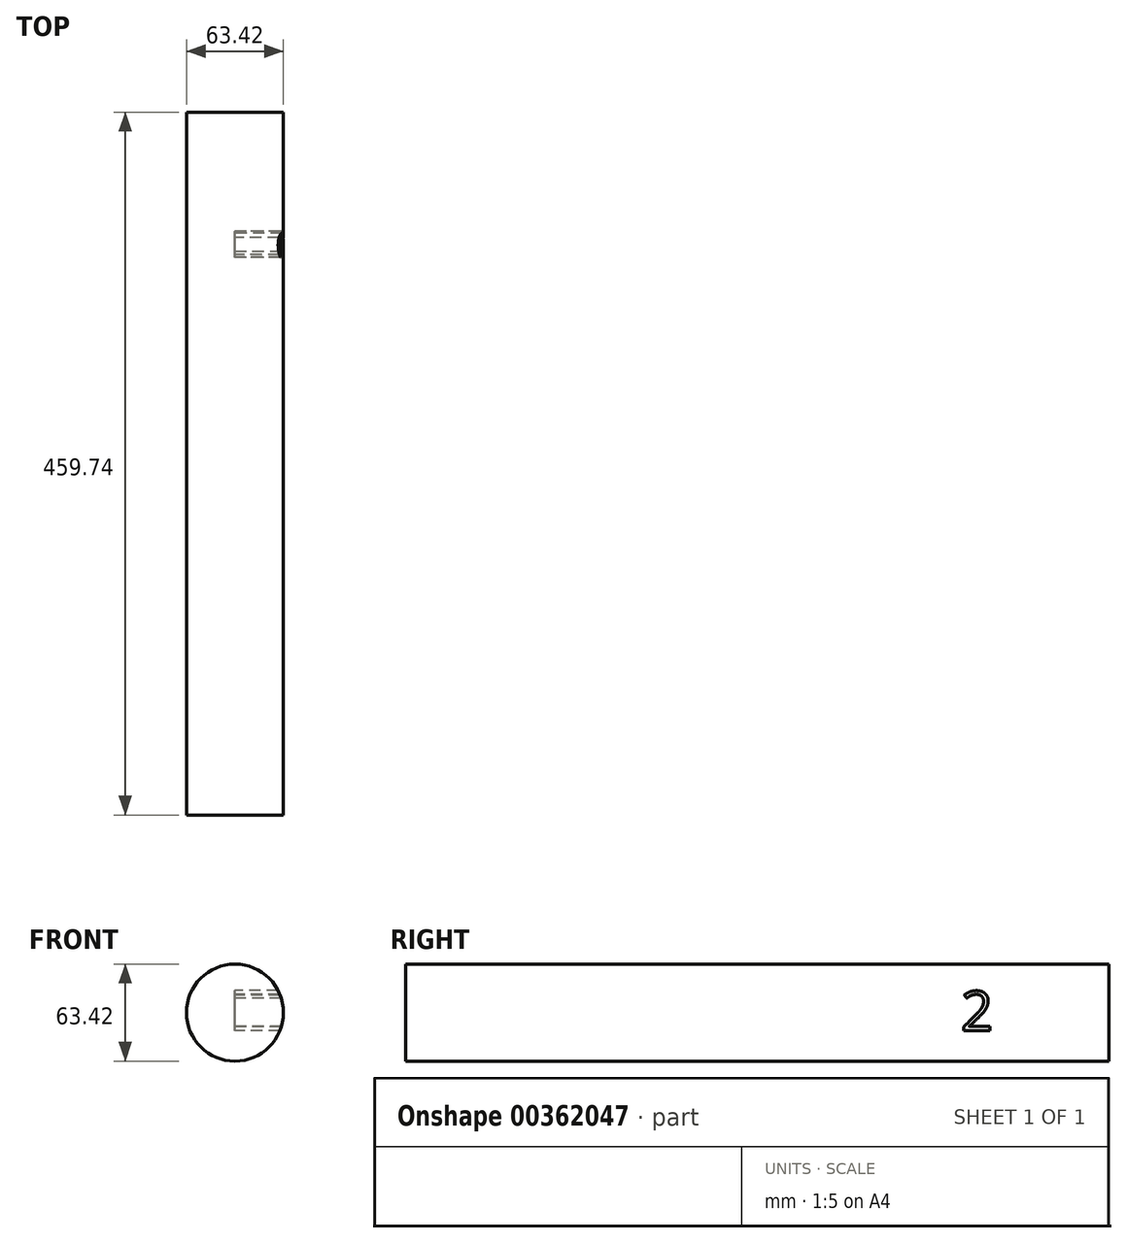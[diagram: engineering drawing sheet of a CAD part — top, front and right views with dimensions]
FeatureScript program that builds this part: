
annotation { "Feature Type Name" : "Feature", "Feature Type Description" : "" }
export const myFeature = defineFeature(function(context is Context, id is Id, definition is map)
    precondition{}
    {
        {
            var Q0;
            Q0=qCreatedBy(makeId("Front.planeOp"),FACE);
            var sketch = newSketch(context, id + "F0", { "sketchPlane" : qUnion([Q0])});
            skCircle(sketch, "E0", {"center": v(0, 0) * mm, "radius": 31.7 * mm});
            skSolve(sketch);
        }
        {
            var Q0;
            Q0 = qSketchRegion(id + "F0", true);
            extrude(context, id + "F1", {"entities" : qUnion([Q0]), "depth" : 459.74 * mm});
        }
        {
            var Q0;
            Q0=qCreatedBy(makeId("Right.planeOp"),FACE);
            var sketch = newSketch(context, id + "F2", { "sketchPlane" : qUnion([Q0])});
            skText(sketch, "E1", { "text": "2", "fontName": "OpenSans-Regular.ttf"});
            const initialGuessF2  = {"E1": [-0.0967, -0.01182, 1, 0, 0.02606]};
            skSetInitialGuess(sketch, initialGuessF2);
            skSolve(sketch);
        }
        {
            var Q0;
            Q0 = qSketchRegion(id + "F2", true);
            extrude(context, id + "F3", {"entities" : qUnion([Q0]), "operationType" : NewBodyOperationType.REMOVE, "depth" : 701.04 * mm});
        }
    });
